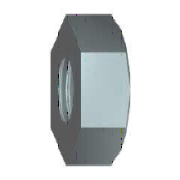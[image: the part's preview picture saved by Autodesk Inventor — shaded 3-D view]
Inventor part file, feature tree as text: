
AUTODESK INVENTOR PART (.ipt)
format: ipt  version: 2024.2 (Build 282272000, 272)  size: 173,568 bytes
history: native  units: mm (DEFAULTED — no unit token found)
features: chamfer x2, plane x2, hole x1, other x1, mirror x1, sketch x1
ambient origin geometry x7: Origin, YZ Plane, XZ Plane, X Axis, Y Axis, Z Axis, Center Point
bodies: Solid1 (feature_tree), Body (feature_tree)
feature tree (8):
  hole  "Thread"  [1 undecoded]
  chamfer  "Chamfer4"  Distance=5.5mm
  chamfer  "Chamfer3"  Angle=30.0deg  [1 undecoded]
  other  "Work Axis1"
  plane  "Work Plane1"
  plane  "Work Plane2"
  mirror  "Mirror1"
  sketch  "Sketch5"  dims[d0=6.350853mm d1=2.4mm d2=0.0mm d3=5.5mm d4=30.0deg d5=90.0deg d6=2.459mm d7=12.7mm d8=9.525mm d9=6.35mm d10=14.3117mm d11=19.05mm d12=20.594885mm d13=0.270633mm d14=30.0deg d20=0.0mm d21=0.270633mm d24=0.0mm d25=0.0mm d31=0.270633mm d32=2.0mm d33=30.0deg]
note: 2 required parameter values undecoded (feature->parameter linkage not recoverable at this tier; creation-order binding heuristic only, values carry confidence <= 0.55)
